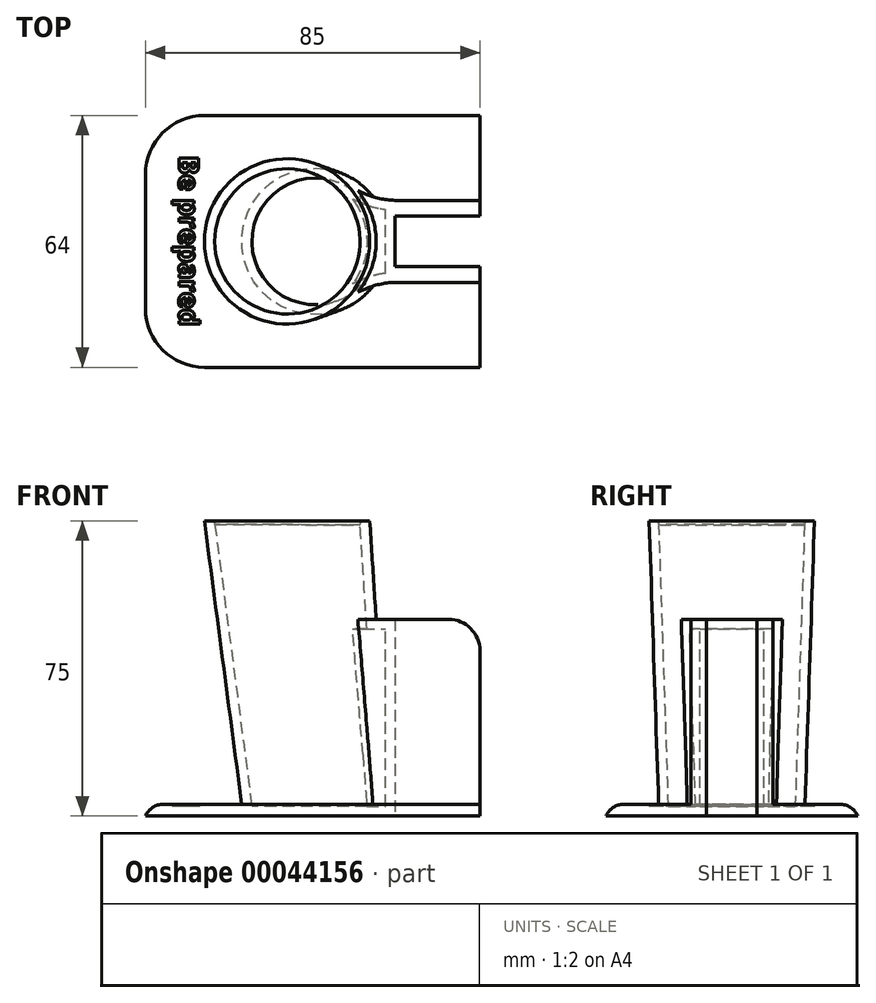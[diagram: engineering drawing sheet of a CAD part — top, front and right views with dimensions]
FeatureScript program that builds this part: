
annotation { "Feature Type Name" : "Feature", "Feature Type Description" : "" }
export const myFeature = defineFeature(function(context is Context, id is Id, definition is map)
    precondition{}
    {
        {
            var Q0;
            Q0=qCreatedBy(makeId("Top.planeOp"),FACE);
            var sketch = newSketch(context, id + "F0", { "sketchPlane" : qUnion([Q0])});
            skPoint(sketch, "E0.middle", {"position": v(0, 0) * mm});
            skCircle(sketch, "E1", {"center": v(-41.62, 0) * mm, "radius": 18.5 * mm});
            skLineSegment(sketch, "E2", {"start": v(-23.12, 34.9) * mm, "end": v(-23.12, -46.32) * mm, "construction": true});
            skLineSegment(sketch, "E3.bottom", {"start": v(-29.57, -14.03) * mm, "end": v(-53.68, -14.03) * mm, "construction": true});
            skLineSegment(sketch, "E3.top", {"start": v(-29.57, 14.03) * mm, "end": v(-53.68, 14.03) * mm, "construction": true});
            skLineSegment(sketch, "E3.left", {"start": v(-29.57, -14.03) * mm, "end": v(-29.57, 14.03) * mm, "construction": true});
            skLineSegment(sketch, "E3.right", {"start": v(-53.68, -14.03) * mm, "end": v(-53.68, 14.03) * mm, "construction": true});
            skPoint(sketch, "E4.MirrorCS.start.orphan", {"position": v(-29.57, -14.03) * mm});
            skSolve(sketch);
        }
        {
            var Q0;
            Q0=qCreatedBy(makeId("Top.planeOp"),FACE);
            cPlane(context, id + "F1", {"entities" : qUnion([Q0]), "cplaneType" : CPlaneType.OFFSET, "offset" : 75 * mm, "width" : 150 * mm, "height" : 150 * mm});
        }
        {
            var Q0;
            Q0=qCreatedBy(id+"F1.planeOp",FACE);
            var sketch = newSketch(context, id + "F2", { "sketchPlane" : qUnion([Q0])});
            skCircle(sketch, "E5", {"center": v(-49, 0) * mm, "radius": 21 * mm});
            skLineSegment(sketch, "E6", {"start": v(-28, 26.97) * mm, "end": v(-28, -33.27) * mm, "construction": true});
            skPoint(sketch, "E7", {"position": v(-33.04, -13.65) * mm});
            skPoint(sketch, "E8.MirrorP", {"position": v(-33.04, 13.65) * mm});
            skLineSegment(sketch, "E9.bottom", {"start": v(-33.04, -13.65) * mm, "end": v(-64.96, -13.65) * mm, "construction": true});
            skLineSegment(sketch, "E9.top", {"start": v(-33.04, 13.65) * mm, "end": v(-64.96, 13.65) * mm, "construction": true});
            skLineSegment(sketch, "E9.left", {"start": v(-33.04, -13.65) * mm, "end": v(-33.04, 13.65) * mm, "construction": true});
            skLineSegment(sketch, "E9.right", {"start": v(-64.96, -13.65) * mm, "end": v(-64.96, 13.65) * mm, "construction": true});
            skSolve(sketch);
        }
        {
            var Q0;
            Q0=makeQuery(id+"F2.imprint","IMPRINT",FACE,{"disambiguationData":[TD([[makeQuery(id+"F2.imprint","IMPRINT",EDGE,{"derivedFrom":sQuery(id+"F2.wireOp",EDGE,"E5")}),1.0]])]});
            var Q1;
            Q1=makeQuery(id+"F0.imprint","IMPRINT",FACE,{"disambiguationData":[TD([[makeQuery(id+"F0.imprint","IMPRINT",EDGE,{"derivedFrom":sQuery(id+"F0.wireOp",EDGE,"E1")}),1.0]])]});
            loft(context, id + "F3", {"sheetProfilesArray" : [{ "sheetProfileEntities" : qUnion([Q0]) }, { "sheetProfileEntities" : qUnion([Q1]) }]});
        }
        {
            var Q0;
            Q0=qCreatedBy(makeId("Top.planeOp"),FACE);
            var sketch = newSketch(context, id + "F4", { "sketchPlane" : qUnion([Q0])});
            skLineSegment(sketch, "E10", {"start": v(-33.48, 13.89) * mm, "end": v(-25.1, 10.42) * mm});
            skLineSegment(sketch, "E11", {"start": v(-33.48, 13.89) * mm, "end": v(-33.48, 0) * mm});
            skLineSegment(sketch, "E12", {"start": v(0, 6.94) * mm, "end": v(0, 6.4) * mm});
            skLineSegment(sketch, "E13.MirrorCS", {"start": v(-33.48, -13.89) * mm, "end": v(-33.48, 0) * mm});
            skLineSegment(sketch, "E14.MirrorCS", {"start": v(-33.48, -13.89) * mm, "end": v(-25.1, -10.42) * mm});
            skLineSegment(sketch, "E15.MirrorCS", {"start": v(0, -6.94) * mm, "end": v(0, -6.4) * mm});
            skLineSegment(sketch, "E16", {"start": v(0, 6.94) * mm, "end": v(0, 32) * mm});
            skLineSegment(sketch, "E17", {"start": v(0, 32) * mm, "end": v(-70, 32) * mm});
            skLineSegment(sketch, "E18", {"start": v(-85, 17) * mm, "end": v(-85, 0) * mm});
            skLineSegment(sketch, "E19.MirrorCS", {"start": v(-85, -17) * mm, "end": v(-85, 0) * mm});
            skLineSegment(sketch, "E20.MirrorCS", {"start": v(0, -32) * mm, "end": v(-70, -32) * mm});
            skLineSegment(sketch, "E21.MirrorCS", {"start": v(0, -6.94) * mm, "end": v(0, -32) * mm});
            skPoint(sketch, "E22.visualSharp", {"position": v(-85, 32) * mm});
            skArc(sketch, "E22.filletArc", {"start": v(-70, 32) * mm, "mid": v(-80.6, 27.6) * mm, "end": v(-85, 17) * mm});
            skPoint(sketch, "E23.visualSharp", {"position": v(-85, -32) * mm});
            skArc(sketch, "E23.filletArc", {"start": v(-85, -17) * mm, "mid": v(-80.6, -27.6) * mm, "end": v(-70, -32) * mm});
            skLineSegment(sketch, "E24", {"start": v(0, 6.4) * mm, "end": v(-21.55, 6.4) * mm});
            skLineSegment(sketch, "E25", {"start": v(-21.55, 6.4) * mm, "end": v(-21.55, 0) * mm});
            skLineSegment(sketch, "E26", {"start": v(-25.1, 10.42) * mm, "end": v(0, 10.42) * mm});
            skLineSegment(sketch, "E27.MirrorCS", {"start": v(0, -6.4) * mm, "end": v(-21.55, -6.4) * mm});
            skLineSegment(sketch, "E28.MirrorCS", {"start": v(-21.55, -6.4) * mm, "end": v(-21.55, 0) * mm});
            skPoint(sketch, "E29.start.orphan", {"position": v(0, 0) * mm});
            skLineSegment(sketch, "E30", {"start": v(-25.1, -10.42) * mm, "end": v(0, -10.42) * mm});
            skSolve(sketch);
        }
        {
            var Q0;
            Q0=makeQuery(id+"F4.imprint","IMPRINT",FACE,{"disambiguationData":[TD([[makeQuery(id+"F4.imprint","IMPRINT",EDGE,{"derivedFrom":sQuery(id+"F4.wireOp",EDGE,"E10")}),-1.0]])]});
            extrude(context, id + "F5", {"entities" : qUnion([Q0]), "operationType" : NewBodyOperationType.ADD, "offsetDistance" : 25 * mm, "depth" : 50 * mm});
        }
        {
            var Q0;
            Q0=makeQuery(id+"F5.opExtrude","SWEPT_EDGE",EDGE,{"disambiguationData":[OSD([sQuery(id+"F4.wireOp",EDGE,"E14.MirrorCS"),sQuery(id+"F4.wireOp",EDGE,"f6d85739-a220-41b5-976d-6718759801bd0.MirrorCS")])]});
            var Q1;
            Q1=makeQuery(id+"F5.opExtrude","SWEPT_EDGE",EDGE,{"disambiguationData":[OSD([sQuery(id+"F4.wireOp",EDGE,"E10"),sQuery(id+"F4.wireOp",EDGE,"rIZNXekO-nN5v-HSPS-u9rq-u1Fm6N6ucfsw")])]});
            fillet(context, id + "F6", {"entities" : qUnion([Q0, Q1]), "radius" : 20 * mm, "tangentPropagation" : true, "allowEdgeOverflow" : false});
        }
        {
            var Q0;
            Q0=makeQuery(id+"F4.imprint","IMPRINT",FACE,{"disambiguationData":[TD([[makeQuery(id+"F4.imprint","IMPRINT",EDGE,{"derivedFrom":sQuery(id+"F4.wireOp",EDGE,"E10")}),1.0]])]});
            extrude(context, id + "F7", {"entities" : qUnion([Q0]), "operationType" : NewBodyOperationType.ADD, "depth" : 3 * mm, "offsetDistance" : 25 * mm});
        }
        {
            var Q0;
            Q0=makeQuery(id+"F3.opLoft","CAP_FACE",FACE,{"disambiguationData":[OSD([makeQuery(id+"F2.imprint","IMPRINT",FACE,{"disambiguationData":[TD([[makeQuery(id+"F2.imprint","IMPRINT",EDGE,{"derivedFrom":sQuery(id+"F2.wireOp",EDGE,"E5")}),1.0]])]})])],"isStart":true});
            shell(context, id + "F8", {"entities" : qUnion([Q0]), "thickness" : 2.5 * mm});
        }
        {
            var Q0;
            Q0=makeQuery(id+"F8.opShell","OFFSET_EDGE",EDGE,{"disambiguationData":[OSD([sQuery(id+"F2.wireOp",EDGE,"E5")])]});
            var Q1;
            Q1=makeQuery(id+"F3.opLoft","MID_CAP_EDGE",EDGE,{"disambiguationData":[OSD([sQuery(id+"F2.wireOp",EDGE,"E5")])],"capPos":0.0});
            fillet(context, id + "F9", {"entities" : qUnion([Q0, Q1]), "radius" : 1 * mm, "tangentPropagation" : true, "allowEdgeOverflow" : false});
        }
        {
            var Q0;
            Q0=makeQuery(id+"F5.opExtrude","CAP_EDGE",EDGE,{"disambiguationData":[OSD([sQuery(id+"F4.wireOp",EDGE,"E15.MirrorCS"),sQuery(id+"F4.wireOp",EDGE,"E21.MirrorCS")])],"isStart":false});
            var Q1;
            Q1=makeQuery(id+"F5.opExtrude","CAP_EDGE",EDGE,{"disambiguationData":[OSD([sQuery(id+"F4.wireOp",EDGE,"E12"),sQuery(id+"F4.wireOp",EDGE,"E16")])],"isStart":false});
            fillet(context, id + "F10", {"entities" : qUnion([Q0, Q1]), "radius" : 8 * mm, "tangentPropagation" : true, "allowEdgeOverflow" : false});
        }
        {
            var Q0;
            Q0=makeQuery(id+"F7.opExtrude","CAP_EDGE",EDGE,{"disambiguationData":[OSD([sQuery(id+"F4.wireOp",EDGE,"E20.MirrorCS")])],"isStart":false});
            var Q1;
            Q1=makeQuery(id+"F7.opExtrude","CAP_EDGE",EDGE,{"disambiguationData":[OSD([sQuery(id+"F4.wireOp",EDGE,"E23.filletArc")])],"isStart":false});
            var Q2;
            Q2=makeQuery(id+"F7.opExtrude","CAP_EDGE",EDGE,{"disambiguationData":[OSD([sQuery(id+"F4.wireOp",EDGE,"E18"),sQuery(id+"F4.wireOp",EDGE,"E19.MirrorCS")])],"isStart":false});
            var Q3;
            Q3=makeQuery(id+"F7.opExtrude","CAP_EDGE",EDGE,{"disambiguationData":[OSD([sQuery(id+"F4.wireOp",EDGE,"E22.filletArc")])],"isStart":false});
            var Q4;
            Q4=makeQuery(id+"F7.opExtrude","CAP_EDGE",EDGE,{"disambiguationData":[OSD([sQuery(id+"F4.wireOp",EDGE,"E17")])],"isStart":false});
            fillet(context, id + "F11", {"entities" : qUnion([Q0, Q1, Q2, Q3, Q4]), "radius" : 5 * mm, "tangentPropagation" : true, "allowEdgeOverflow" : false});
        }
        {
            var Q0;
            Q0=makeQuery(id+"F7.opExtrude","CAP_FACE",FACE,{"disambiguationData":[OSD([sQuery(id+"F4.wireOp",EDGE,"E10"),sQuery(id+"F4.wireOp",EDGE,"E11"),sQuery(id+"F4.wireOp",EDGE,"E13.MirrorCS"),sQuery(id+"F4.wireOp",EDGE,"E14.MirrorCS"),sQuery(id+"F4.wireOp",EDGE,"E16"),sQuery(id+"F4.wireOp",EDGE,"E17"),sQuery(id+"F4.wireOp",EDGE,"E18"),sQuery(id+"F4.wireOp",EDGE,"E19.MirrorCS"),sQuery(id+"F4.wireOp",EDGE,"E20.MirrorCS"),sQuery(id+"F4.wireOp",EDGE,"E21.MirrorCS"),sQuery(id+"F4.wireOp",EDGE,"E22.filletArc"),sQuery(id+"F4.wireOp",EDGE,"E23.filletArc"),sQuery(id+"F4.wireOp",EDGE,"E26"),sQuery(id+"F4.wireOp",EDGE,"E30")])],"isStart":false});
            var sketch = newSketch(context, id + "F12", { "sketchPlane" : qUnion([Q0])});
            skText(sketch, "E31", { "text": "Be prepared", "fontName": "OpenSans-Bold.ttf"});
            const initialGuessF12  = {"E31": [-0.07648, 0.02176, 0, -1, 0.0051]};
            skSetInitialGuess(sketch, initialGuessF12);
            skSolve(sketch);
        }
        {
            var Q0;
            Q0=makeQuery(id+"F12.imprint","IMPRINT",FACE,{"disambiguationData":[TD([[makeQuery(id+"F12.imprint","IMPRINT",EDGE,{"derivedFrom":sQuery(id+"F12.wireOp",EDGE,"E31.sketch_text.stroke-0")}),-1.0]])]});
            var Q1;
            Q1=makeQuery(id+"F12.imprint","IMPRINT",FACE,{"disambiguationData":[TD([[makeQuery(id+"F12.imprint","IMPRINT",EDGE,{"derivedFrom":sQuery(id+"F12.wireOp",EDGE,"E31.sketch_text.stroke-25")}),-1.0]])]});
            var Q2;
            Q2=makeQuery(id+"F12.imprint","IMPRINT",FACE,{"disambiguationData":[TD([[makeQuery(id+"F12.imprint","IMPRINT",EDGE,{"derivedFrom":sQuery(id+"F12.wireOp",EDGE,"E31.sketch_text.stroke-45")}),-1.0]])]});
            var Q3;
            Q3=makeQuery(id+"F12.imprint","IMPRINT",FACE,{"disambiguationData":[TD([[makeQuery(id+"F12.imprint","IMPRINT",EDGE,{"derivedFrom":sQuery(id+"F12.wireOp",EDGE,"E31.sketch_text.stroke-68")}),-1.0]])]});
            var Q4;
            Q4=makeQuery(id+"F12.imprint","IMPRINT",FACE,{"disambiguationData":[TD([[makeQuery(id+"F12.imprint","IMPRINT",EDGE,{"derivedFrom":sQuery(id+"F12.wireOp",EDGE,"E31.sketch_text.stroke-81")}),-1.0]])]});
            var Q5;
            Q5=makeQuery(id+"F12.imprint","IMPRINT",FACE,{"disambiguationData":[TD([[makeQuery(id+"F12.imprint","IMPRINT",EDGE,{"derivedFrom":sQuery(id+"F12.wireOp",EDGE,"E31.sketch_text.stroke-101")}),-1.0]])]});
            var Q6;
            Q6=makeQuery(id+"F12.imprint","IMPRINT",FACE,{"disambiguationData":[TD([[makeQuery(id+"F12.imprint","IMPRINT",EDGE,{"derivedFrom":sQuery(id+"F12.wireOp",EDGE,"E31.sketch_text.stroke-124")}),-1.0]])]});
            var Q7;
            Q7=makeQuery(id+"F12.imprint","IMPRINT",FACE,{"disambiguationData":[TD([[makeQuery(id+"F12.imprint","IMPRINT",EDGE,{"derivedFrom":sQuery(id+"F12.wireOp",EDGE,"E31.sketch_text.stroke-149")}),-1.0]])]});
            var Q8;
            Q8=makeQuery(id+"F12.imprint","IMPRINT",FACE,{"disambiguationData":[TD([[makeQuery(id+"F12.imprint","IMPRINT",EDGE,{"derivedFrom":sQuery(id+"F12.wireOp",EDGE,"E31.sketch_text.stroke-162")}),-1.0]])]});
            var Q9;
            Q9=makeQuery(id+"F12.imprint","IMPRINT",FACE,{"disambiguationData":[TD([[makeQuery(id+"F12.imprint","IMPRINT",EDGE,{"derivedFrom":sQuery(id+"F12.wireOp",EDGE,"E31.sketch_text.stroke-182")}),-1.0]])]});
            extrude(context, id + "F13", {"entities" : qUnion([Q0, Q1, Q2, Q3, Q4, Q5, Q6, Q7, Q8, Q9]), "operationType" : NewBodyOperationType.REMOVE, "oppositeDirection" : true, "depth" : .4 * mm});
        }
    });
